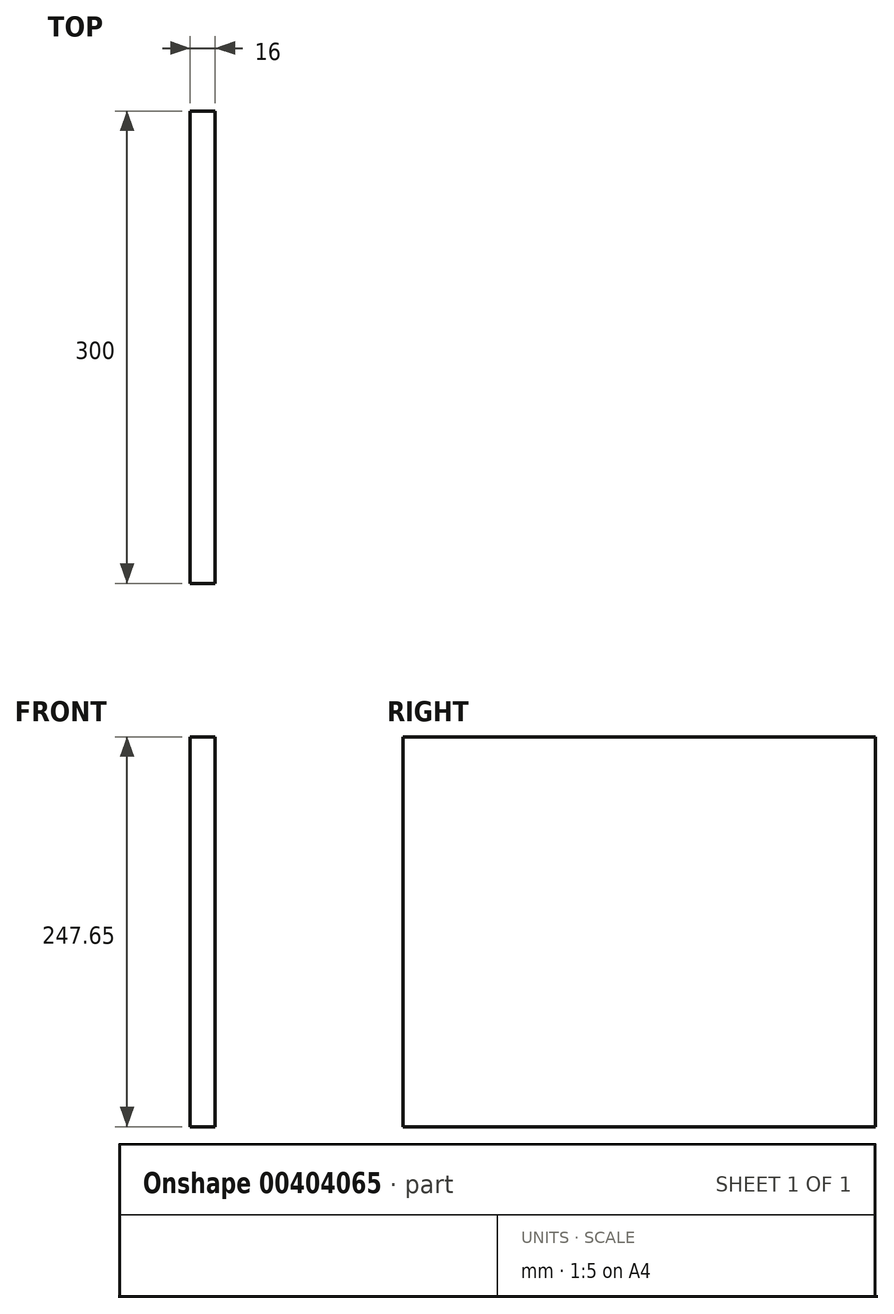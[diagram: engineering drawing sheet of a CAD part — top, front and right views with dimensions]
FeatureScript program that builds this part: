
annotation { "Feature Type Name" : "Feature", "Feature Type Description" : "" }
export const myFeature = defineFeature(function(context is Context, id is Id, definition is map)
    precondition{}
    {
        {
            var Q0;
            Q0=qCreatedBy(makeId("Right.planeOp"),FACE);
            var sketch = newSketch(context, id + "F0", { "sketchPlane" : qUnion([Q0])});
            skLineSegment(sketch, "E0.bottom", {"start": v(-156.14, 119.72) * mm, "end": v(143.86, 119.72) * mm});
            skLineSegment(sketch, "E0.top", {"start": v(-156.14, -127.93) * mm, "end": v(143.86, -127.93) * mm});
            skLineSegment(sketch, "E0.left", {"start": v(-156.14, 119.72) * mm, "end": v(-156.14, -127.93) * mm});
            skLineSegment(sketch, "E0.right", {"start": v(143.86, 119.72) * mm, "end": v(143.86, -127.93) * mm});
            skSolve(sketch);
        }
        {
            var Q0;
            Q0 = qSketchRegion(id + "F0", true);
            extrude(context, id + "F1", {"entities" : qUnion([Q0]), "depth" : 16 * mm});
        }
    });
